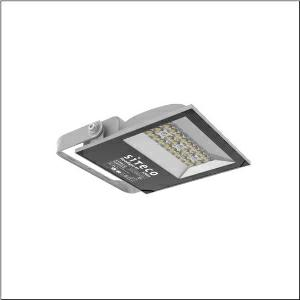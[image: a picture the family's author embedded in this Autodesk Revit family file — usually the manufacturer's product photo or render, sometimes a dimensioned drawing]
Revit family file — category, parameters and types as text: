
# Revit family: floodlight_fl_41_mini___pl32_5xa8571a1121_0023
name_source: partatom
category: Lighting Fixtures
units: mm (PartAtom-declared; Revit-internal decimal feet)

## family parameters
Cut with Voids When Loaded = No
Host = Face
Light Source = No
Part Type = Normal
Room Calculation Point = No
Round Connector Dimension = Use Diameter
Shared = No

## types (1)
- --- (1 x LED, 13000 lm, 100 W, 3000K)
    Apparent Load = 100 VA
    CIE Flux Codes = 40 79 99 100 100
    Color Rendering = 70
    Color Temperature = 3000K
    Default Elevation = 1800 mm
    Description = Floodlight FL 41 mini, floodlight, primary light control with lens, of PMMA, primary optical cover: protective disc, transparent, light distribution: PL32, light emission: direct distribution, installation type: surface-mounted, LED, High Power LED, rated luminous flux: 13.000lm, luminous efficacy: 130lm/W, light colour: 730, colour temperature: 3000K, control gear: ON/OFF Multilumen, with cable, 3x 1.5mm², mains connection: 220..240V, AC, 50/60Hz, connection cable pre-assembled, cable length: 2m, rated input power: 100W, luminaire housing, of diecast aluminium, powder-coated, metallic grey (RAL 9006), length: 265mm, width: 245mm, height: 54mm, protection rating (complete): IP65, insulation class (complete): insulation class I (protective earthing), certification: CE, ENEC, impact resistance: IK08, permissible operating ambient temperature: -40..+40°C, permissible storage temperature: -40..+60°C, packaging unit: 1 piece

Light Distribution: PL32
    Height = 54 mm
    Lamp = 1 x LED
    Lamp Light Flux = 13000 lm
    Lamp Power = 100 W
    Lamp count = 1
    Length = 226 mm
    Luminous efficacy = 130 lm/W
    Manufacturer = Siteco
    ModVariant = No
    Model = 5XA8571A1121
    Mounting Place = Ceiling
    Mounting Type = Surface mounted
    Number of Poles = 1
    OnlyDefault = Yes
    Power Factor = 1
    Product Name = Floodlight FL 41 mini | PL32
    Product group = floodlight | ceiling mounted
    ProductGroupID = 305
    Protection Class = Protection class I
    Protection Degree = IP 65
    RLX_Detail_Level = 1
    RLX_Emergency_Light_Flux = 0 lm
    RLX_Emergency_Type = 0
    RLX_Emergency_Type_DB = No
    RlxData = <blob elided: 24629 chars, md5=a4fba3a3>
    Socket = socket
    Standby Power = 0 W
    System Light Flux = 13000 lm
    System Power = 100 W
    Type Comments = factory setting: luminous flux: 100 % | (OFF | OFF | OFF)
    Type Image = l_1248226.jpg
    URL = http://relux.com
    VarID = @adj_132773
    Voltage = 0 V
    Weight = 0.00 kg
    Width = 241 mm

## geometry (parser evidence)
native form markers: Blend x4, Sweep x11
no freeform markers — native parametric forms only
